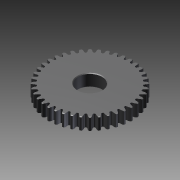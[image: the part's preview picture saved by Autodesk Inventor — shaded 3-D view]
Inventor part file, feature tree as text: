
AUTODESK INVENTOR PART (.ipt)
format: ipt  version: 2016 (Build 200138000, 138)  size: 1,212,416 bytes
history: native  units: mm
features: other x14, revolve x3, sketch x3, extrude x1, hole x1
ambient origin geometry x8: Origin, YZ Plane, XZ Plane, XY Plane, X Axis, Y Axis, Z Axis, Center Point
bodies: Solid1 (feature_tree)
feature tree (22):
  revolve  "Revolution1"  [1 undecoded]
  extrude  "Extrusion1"  TaperAngle=360.0deg  [1 undecoded]
  hole  "Hole1"  [1 undecoded]
  revolve  "Revolution2"  [1 undecoded]
  revolve  "Revolution3"  [1 undecoded]
  other  "b_XY"
  other  "b_YZ"
  other  "b_ZX"
  other  "b_X"
  other  "b_Y"
  other  "b_Z"
  other  "b_Center"
  other  "turn_around_XY"
  other  "turn_around_YZ"
  other  "turn_around_ZX"
  other  "turn_around_X"
  other  "turn_around_Y"
  other  "turn_around_Z"
  other  "turn_around_Center"
  sketch  "Sketch_12"  dims[d11=360.0deg d12=0.0mm]
  sketch  "Sketch_3"  dims[d0=360.0deg d1=6.0mm d2=0.0mm]
  sketch  "Sketch3"  dims[d3=12.0mm d4=6.0mm d5=4.0mm d6=2.0mm d7=90.0deg d8=6.0mm d9=0.0mm d10=360.0deg]
note: 5 required parameter values undecoded (feature->parameter linkage not recoverable at this tier; creation-order binding heuristic only, values carry confidence <= 0.55)